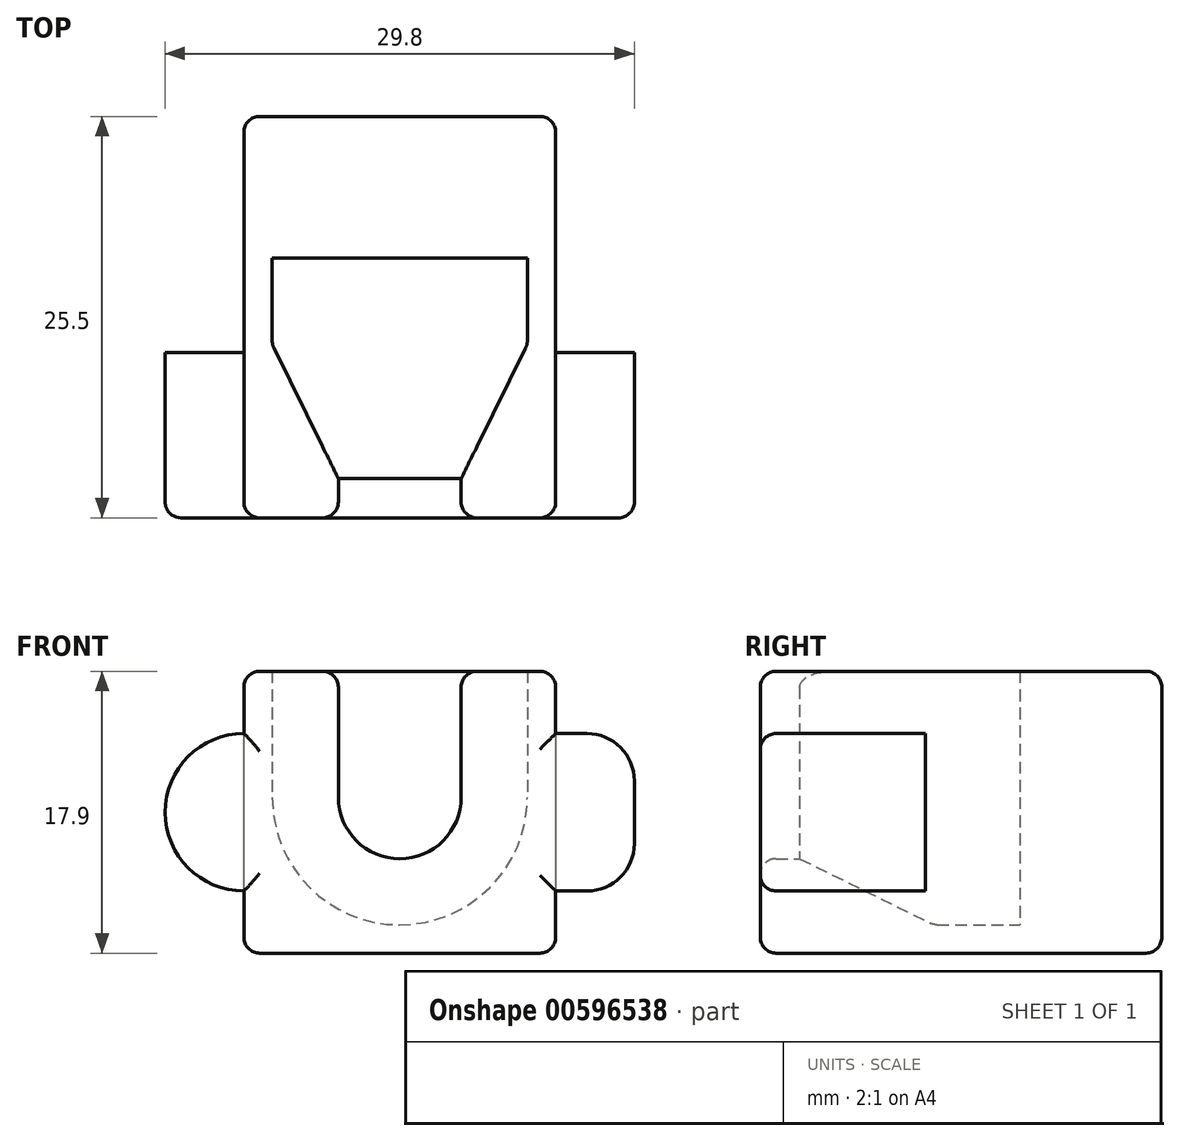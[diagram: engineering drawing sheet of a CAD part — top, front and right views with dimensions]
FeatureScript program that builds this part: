
annotation { "Feature Type Name" : "Feature", "Feature Type Description" : "" }
export const myFeature = defineFeature(function(context is Context, id is Id, definition is map)
    precondition{}
    {
        {
            var Q0;
            Q0=qCreatedBy(makeId("Top.planeOp"),FACE);
            var sketch = newSketch(context, id + "F0", { "sketchPlane" : qUnion([Q0])});
            skLineSegment(sketch, "E0", {"start": v(-9.9, 0) * mm, "end": v(-3.9, 0) * mm});
            skLineSegment(sketch, "E1", {"start": v(-3.9, 0) * mm, "end": v(-3.9, 2.5) * mm});
            skLineSegment(sketch, "E2", {"start": v(-3.9, 2.5) * mm, "end": v(-8.1, 11) * mm});
            skLineSegment(sketch, "E3", {"start": v(-8.1, 11) * mm, "end": v(-8.1, 16.5) * mm});
            skLineSegment(sketch, "E4", {"start": v(-8.1, 16.5) * mm, "end": v(0, 16.5) * mm});
            skLineSegment(sketch, "E5", {"start": v(0, 16.5) * mm, "end": v(0, 18.5) * mm});
            skLineSegment(sketch, "E6", {"start": v(0, 18.5) * mm, "end": v(-9.9, 18.5) * mm});
            skLineSegment(sketch, "E7", {"start": v(-9.9, 18.5) * mm, "end": v(-9.9, 0) * mm});
            skLineSegment(sketch, "E8", {"start": v(0, 44.18) * mm, "end": v(0, -54.71) * mm, "construction": true});
            skSolve(sketch);
        }
        {
            var Q0;
            Q0=makeQuery(id+"F0.imprint","IMPRINT",FACE,{"disambiguationData":[TD([[makeQuery(id+"F0.imprint","IMPRINT",EDGE,{"derivedFrom":sQuery(id+"F0.wireOp",EDGE,"E0")}),1.0]])]});
            var Q1;
            Q1=sQuery(id+"F0.wireOp",EDGE,"E8");
            revolve(context, id + "F1", {"entities" : qUnion([Q0]), "axis" : qUnion([Q1]), "revolveType" : RevolveType.ONE_DIRECTION, "angle" : 180 * degree});
        }
        {
            var Q0;
            Q0=makeQuery(id+"F1.opRevolve","SWEPT_FACE",FACE,{"disambiguationData":[OSD([sQuery(id+"F0.wireOp",EDGE,"E6")])]});
            var sketch = newSketch(context, id + "F2", { "sketchPlane" : qUnion([Q0])});
            skLineSegment(sketch, "E9", {"start": v(-9.9, 0) * mm, "end": v(-9.9, -9.9) * mm});
            skPoint(sketch, "E9.endSnap0", {"position": v(0, -9.9) * mm});
            skLineSegment(sketch, "E10", {"start": v(-9.9, -9.9) * mm, "end": v(9.9, -9.9) * mm});
            skLineSegment(sketch, "E11", {"start": v(9.9, -9.9) * mm, "end": v(9.9, 0) * mm});
            skSolve(sketch);
        }
        {
            var Q0;
            {var subQ0=sQuery(id+"F2.wireOp",EDGE,"E9");Q0=makeQuery(id+"F2.imprint","IMPRINT",FACE,{"disambiguationData":[TD([[makeQuery(id+"F2.imprint","IMPRINT",EDGE,{"derivedFrom":subQ0}),1.0]])]});}
            var Q1;
            {var subQ0=sQuery(id+"F2.wireOp",EDGE,"E11");Q1=makeQuery(id+"F2.imprint","IMPRINT",FACE,{"disambiguationData":[TD([[makeQuery(id+"F2.imprint","IMPRINT",EDGE,{"derivedFrom":subQ0}),1.0]])]});}
            var Q2;
            Q2=makeQuery(id+"F1.opRevolve","SWEPT_FACE",FACE,{"disambiguationData":[OSD([sQuery(id+"F0.wireOp",EDGE,"E0")])]});
            extrude(context, id + "F3", {"entities" : qUnion([Q0, Q1]), "operationType" : NewBodyOperationType.ADD, "endBound" : BoundingType.UP_TO_SURFACE, "oppositeDirection" : true, "depth" : 17 * mm, "endBoundEntityFace" : qUnion([Q2]), "offsetDistance" : 25 * mm});
        }
        {
            var Q0;
            Q0=makeQuery(id+"F1.opRevolve","CAP_FACE",FACE,{"disambiguationData":[OSD([sQuery(id+"F0.wireOp",EDGE,"E0"),sQuery(id+"F0.wireOp",EDGE,"E1"),sQuery(id+"F0.wireOp",EDGE,"E2"),sQuery(id+"F0.wireOp",EDGE,"E3"),sQuery(id+"F0.wireOp",EDGE,"E4"),sQuery(id+"F0.wireOp",EDGE,"E5"),sQuery(id+"F0.wireOp",EDGE,"E6"),sQuery(id+"F0.wireOp",EDGE,"E7")])],"isStart":false});
            extrude(context, id + "F4", {"entities" : qUnion([Q0]), "operationType" : NewBodyOperationType.ADD, "depth" : 8 * mm, "offsetDistance" : 25 * mm});
        }
        {
            var Q0;
            {var subQ0=sQuery(id+"F0.wireOp",EDGE,"E6");var subQ1=sQuery(id+"F2.wireOp",EDGE,"E10");var subQ2=sQuery(id+"F0.wireOp",EDGE,"E7");Q0=makeQuery(id+"F4.boolean.opBoolean","MERGE",FACE,{"derivedFrom":[makeQuery(id+"F3.boolean.opBoolean","MERGE",FACE,{"derivedFrom":[makeQuery(id+"F1.opRevolve","SWEPT_FACE",FACE,{"disambiguationData":[OSD([subQ0])]}),makeQuery(id+"F3.opExtrude","CAP_FACE",FACE,{"disambiguationData":[OSD([subQ0,subQ2,sQuery(id+"F2.wireOp",EDGE,"E9"),subQ1])],"isStart":true}),makeQuery(id+"F3.opExtrude","CAP_FACE",FACE,{"disambiguationData":[OSD([subQ0,subQ2,subQ1,sQuery(id+"F2.wireOp",EDGE,"E11")])],"isStart":true})]}),makeQuery(id+"F4.opExtrude","SWEPT_FACE",FACE,{"disambiguationData":[OSD([subQ0])]})]});}
            var sketch = newSketch(context, id + "F5", { "sketchPlane" : qUnion([Q0])});
            skCircle(sketch, "E12", {"center": v(9.9, -0.95) * mm, "radius": 5 * mm});
            skLineSegment(sketch, "E13.bottom", {"start": v(-11.9, 4.05) * mm, "end": v(-4.9, 4.05) * mm});
            skLineSegment(sketch, "E13.top", {"start": v(-11.9, -5.95) * mm, "end": v(-4.9, -5.95) * mm});
            skLineSegment(sketch, "E13.left", {"start": v(-14.9, 1.05) * mm, "end": v(-14.9, -2.95) * mm});
            skLineSegment(sketch, "E13.right", {"start": v(-4.9, 4.05) * mm, "end": v(-4.9, -5.95) * mm});
            skPoint(sketch, "E13.middle", {"position": v(-9.9, -0.95) * mm});
            skPoint(sketch, "E14.visualSharp", {"position": v(-14.9, -5.95) * mm});
            skArc(sketch, "E14.filletArc", {"start": v(-14.9, -2.95) * mm, "mid": v(-14.02, -5.07) * mm, "end": v(-11.9, -5.95) * mm});
            skPoint(sketch, "E15.visualSharp", {"position": v(-14.9, 4.05) * mm});
            skArc(sketch, "E15.filletArc", {"start": v(-11.9, 4.05) * mm, "mid": v(-14.02, 3.17) * mm, "end": v(-14.9, 1.05) * mm});
            skSolve(sketch);
        }
        {
            var Q0;
            {var subQ0=sQuery(id+"F5.wireOp",EDGE,"E12");var subQ1=sQuery(id+"F2.wireOp",EDGE,"E11");var subQ2=makeQuery(id+"F4.boolean.opBoolean","MERGE",EDGE,{"derivedFrom":[makeQuery(id+"F3.opExtrude","CAP_EDGE",EDGE,{"disambiguationData":[OSD([subQ1])],"isStart":true}),makeQuery(id+"F4.opExtrude","SWEPT_EDGE",EDGE,{"disambiguationData":[OSD([sQuery(id+"F0.wireOp",EDGE,"E6"),sQuery(id+"F0.wireOp",EDGE,"E7"),subQ1])]})]});var subQ3=makeQuery(id+"F5.imprint","INTERSECT",VERTEX,{"disambiguationData":[OD(0.0)],"derivedFrom":[subQ2,subQ0]});Q0=makeQuery(id+"F5.imprint","IMPRINT",FACE,{"disambiguationData":[TD([[makeQuery(id+"F5.imprint","IMPRINT",EDGE,{"disambiguationData":[TD([[subQ3,-1.0]])],"derivedFrom":subQ0}),1.0]])]});}
            var Q1;
            Q1=makeQuery(id+"F5.imprint","IMPRINT",FACE,{"disambiguationData":[TD([[makeQuery(id+"F5.imprint","IMPRINT",EDGE,{"derivedFrom":sQuery(id+"F5.wireOp",EDGE,"E13.left")}),1.0]])]});
            var Q2;
            {var subQ0=sQuery(id+"F0.wireOp",EDGE,"E0");Q2=makeQuery(id+"F4.boolean.opBoolean","MERGE",FACE,{"derivedFrom":[makeQuery(id+"F3.boolean.opBoolean","MERGE",FACE,{"derivedFrom":[makeQuery(id+"F1.opRevolve","SWEPT_FACE",FACE,{"disambiguationData":[OSD([subQ0])]}),makeQuery(id+"F3.opExtrude","CAP_FACE",FACE,{"disambiguationData":[OSD([subQ0]),OD(0.0)],"isStart":false}),makeQuery(id+"F3.opExtrude","CAP_FACE",FACE,{"disambiguationData":[OSD([subQ0]),OD(1.0)],"isStart":false})]}),makeQuery(id+"F4.opExtrude","SWEPT_FACE",FACE,{"disambiguationData":[OSD([subQ0]),TDD([makeQuery(id+"F1.opRevolve","CAP_EDGE",EDGE,{"disambiguationData":[OSD([subQ0])],"isStart":true})])]}),makeQuery(id+"F4.opExtrude","SWEPT_FACE",FACE,{"disambiguationData":[OSD([subQ0]),TDD([makeQuery(id+"F1.opRevolve","CAP_EDGE",EDGE,{"disambiguationData":[OSD([subQ0])],"isStart":false})])]})]});}
            extrude(context, id + "F6", {"entities" : qUnion([Q0, Q1]), "operationType" : NewBodyOperationType.ADD, "endBound" : BoundingType.UP_TO_SURFACE, "oppositeDirection" : true, "depth" : 25 * mm, "endBoundEntityFace" : qUnion([Q2]), "offsetDistance" : 25 * mm});
        }
        {
            var Q0;
            {var subQ0=sQuery(id+"F5.wireOp",EDGE,"E12");var subQ1=sQuery(id+"F2.wireOp",EDGE,"E11");var subQ2=makeQuery(id+"F4.boolean.opBoolean","MERGE",EDGE,{"derivedFrom":[makeQuery(id+"F3.opExtrude","CAP_EDGE",EDGE,{"disambiguationData":[OSD([subQ1])],"isStart":true}),makeQuery(id+"F4.opExtrude","SWEPT_EDGE",EDGE,{"disambiguationData":[OSD([sQuery(id+"F0.wireOp",EDGE,"E6"),sQuery(id+"F0.wireOp",EDGE,"E7"),subQ1])]})]});var subQ3=makeQuery(id+"F5.imprint","INTERSECT",VERTEX,{"disambiguationData":[OD(0.0)],"derivedFrom":[subQ2,subQ0]});Q0=makeQuery(id+"F5.imprint","IMPRINT",FACE,{"disambiguationData":[TD([[makeQuery(id+"F5.imprint","IMPRINT",EDGE,{"disambiguationData":[TD([[subQ3,-1.0]])],"derivedFrom":subQ0}),1.0]])]});}
            var Q1;
            Q1=makeQuery(id+"F5.imprint","IMPRINT",FACE,{"disambiguationData":[TD([[makeQuery(id+"F5.imprint","IMPRINT",EDGE,{"derivedFrom":sQuery(id+"F5.wireOp",EDGE,"E13.left")}),1.0]])]});
            extrude(context, id + "F7", {"entities" : qUnion([Q0, Q1]), "operationType" : NewBodyOperationType.REMOVE, "oppositeDirection" : true, "depth" : 8 * mm, "offsetDistance" : 25 * mm});
        }
        {
            var Q0;
            {var subQ0=sQuery(id+"F5.wireOp",EDGE,"E12");var subQ1=sQuery(id+"F2.wireOp",EDGE,"E11");var subQ2=makeQuery(id+"F4.boolean.opBoolean","MERGE",EDGE,{"derivedFrom":[makeQuery(id+"F3.opExtrude","CAP_EDGE",EDGE,{"disambiguationData":[OSD([subQ1])],"isStart":true}),makeQuery(id+"F4.opExtrude","SWEPT_EDGE",EDGE,{"disambiguationData":[OSD([sQuery(id+"F0.wireOp",EDGE,"E6"),sQuery(id+"F0.wireOp",EDGE,"E7"),subQ1])]})]});var subQ3=makeQuery(id+"F5.imprint","INTERSECT",VERTEX,{"disambiguationData":[OD(0.0)],"derivedFrom":[subQ2,subQ0]});Q0=makeQuery(id+"F5.imprint","IMPRINT",FACE,{"disambiguationData":[TD([[makeQuery(id+"F5.imprint","IMPRINT",EDGE,{"disambiguationData":[TD([[subQ3,1.0]])],"derivedFrom":subQ0}),1.0]])]});}
            var Q1;
            {var subQ0=sQuery(id+"F5.wireOp",EDGE,"E13.right");Q1=makeQuery(id+"F5.imprint","IMPRINT",FACE,{"disambiguationData":[TD([[makeQuery(id+"F5.imprint","IMPRINT",EDGE,{"derivedFrom":subQ0}),1.0]])]});}
            var Q2;
            {var subQ0=sQuery(id+"F5.wireOp",EDGE,"E13.right");Q2=makeQuery(id+"F5.imprint","IMPRINT",FACE,{"disambiguationData":[TD([[makeQuery(id+"F5.imprint","IMPRINT",EDGE,{"derivedFrom":subQ0}),-1.0]])]});}
            extrude(context, id + "F8", {"entities" : qUnion([Q0, Q1, Q2]), "operationType" : NewBodyOperationType.ADD, "depth" : 7 * mm, "offsetDistance" : 25 * mm});
        }
        {
            var Q0;
            Q0=makeQuery(id+"F4.opExtrude","CAP_EDGE",EDGE,{"disambiguationData":[OSD([sQuery(id+"F0.wireOp",EDGE,"E6"),sQuery(id+"F0.wireOp",EDGE,"E7"),sQuery(id+"F2.wireOp",EDGE,"E9")])],"isStart":false});
            var Q1;
            Q1=makeQuery(id+"F4.opExtrude","CAP_EDGE",EDGE,{"disambiguationData":[OSD([sQuery(id+"F0.wireOp",EDGE,"E6"),sQuery(id+"F0.wireOp",EDGE,"E7"),sQuery(id+"F2.wireOp",EDGE,"E11")])],"isStart":false});
            var Q2;
            Q2=makeQuery(id+"F3.opExtrude","SWEPT_EDGE",EDGE,{"disambiguationData":[OSD([sQuery(id+"F2.wireOp",EDGE,"E9"),sQuery(id+"F2.wireOp",EDGE,"E10")])]});
            var Q3;
            Q3=makeQuery(id+"F3.opExtrude","SWEPT_EDGE",EDGE,{"disambiguationData":[OSD([sQuery(id+"F2.wireOp",EDGE,"E10"),sQuery(id+"F2.wireOp",EDGE,"E11")])]});
            var Q4;
            {var subQ0=sQuery(id+"F0.wireOp",EDGE,"E0");Q4=makeQuery(id+"F4.opExtrude","CAP_EDGE",EDGE,{"disambiguationData":[OSD([subQ0]),TDD([makeQuery(id+"F1.opRevolve","CAP_EDGE",EDGE,{"disambiguationData":[OSD([subQ0])],"isStart":false})])],"isStart":false});}
            var Q5;
            {var subQ0=sQuery(id+"F0.wireOp",EDGE,"E0");Q5=makeQuery(id+"F4.opExtrude","CAP_EDGE",EDGE,{"disambiguationData":[OSD([subQ0]),TDD([makeQuery(id+"F1.opRevolve","CAP_EDGE",EDGE,{"disambiguationData":[OSD([subQ0])],"isStart":true})])],"isStart":false});}
            var Q6;
            {var subQ0=sQuery(id+"F2.wireOp",EDGE,"E9");Q6=makeQuery(id+"F4.boolean.opBoolean","MERGE",EDGE,{"derivedFrom":[makeQuery(id+"F3.opExtrude","CAP_EDGE",EDGE,{"disambiguationData":[OSD([subQ0])],"isStart":false}),makeQuery(id+"F4.opExtrude","SWEPT_EDGE",EDGE,{"disambiguationData":[OSD([sQuery(id+"F0.wireOp",EDGE,"E0"),sQuery(id+"F0.wireOp",EDGE,"E6"),sQuery(id+"F0.wireOp",EDGE,"E7"),subQ0])]})]});}
            var Q7;
            {var subQ0=sQuery(id+"F2.wireOp",EDGE,"E11");Q7=makeQuery(id+"F4.boolean.opBoolean","MERGE",EDGE,{"derivedFrom":[makeQuery(id+"F3.opExtrude","CAP_EDGE",EDGE,{"disambiguationData":[OSD([subQ0])],"isStart":false}),makeQuery(id+"F4.opExtrude","SWEPT_EDGE",EDGE,{"disambiguationData":[OSD([sQuery(id+"F0.wireOp",EDGE,"E0"),sQuery(id+"F0.wireOp",EDGE,"E6"),sQuery(id+"F0.wireOp",EDGE,"E7"),subQ0])]})]});}
            var Q8;
            {var subQ0=sQuery(id+"F2.wireOp",EDGE,"E10");Q8=makeQuery(id+"F3.boolean.opBoolean","MERGE",EDGE,{"derivedFrom":[makeQuery(id+"F3.opExtrude","CAP_EDGE",EDGE,{"disambiguationData":[OSD([subQ0]),TDD([makeQuery(id+"F2.imprint","IMPRINT",EDGE,{"disambiguationData":[TD([[makeQuery(id+"F2.imprint","INTERSECT",VERTEX,{"derivedFrom":[sQuery(id+"F2.wireOp",EDGE,"E9"),subQ0]}),-1.0]])],"derivedFrom":subQ0})])],"isStart":false}),makeQuery(id+"F3.opExtrude","CAP_EDGE",EDGE,{"disambiguationData":[OSD([subQ0]),TDD([makeQuery(id+"F2.imprint","IMPRINT",EDGE,{"disambiguationData":[TD([[makeQuery(id+"F2.imprint","INTERSECT",VERTEX,{"derivedFrom":[subQ0,sQuery(id+"F2.wireOp",EDGE,"E11")]}),1.0]])],"derivedFrom":subQ0})])],"isStart":false})]});}
            var Q9;
            {var subQ0=sQuery(id+"F0.wireOp",EDGE,"E6");var subQ1=sQuery(id+"F2.wireOp",EDGE,"E10");var subQ2=sQuery(id+"F0.wireOp",EDGE,"E7");Q9=makeQuery(id+"F4.boolean.opBoolean","MERGE",FACE,{"derivedFrom":[makeQuery(id+"F3.boolean.opBoolean","MERGE",FACE,{"derivedFrom":[makeQuery(id+"F1.opRevolve","SWEPT_FACE",FACE,{"disambiguationData":[OSD([subQ0])]}),makeQuery(id+"F3.opExtrude","CAP_FACE",FACE,{"disambiguationData":[OSD([subQ0,subQ2,sQuery(id+"F2.wireOp",EDGE,"E9"),subQ1])],"isStart":true}),makeQuery(id+"F3.opExtrude","CAP_FACE",FACE,{"disambiguationData":[OSD([subQ0,subQ2,subQ1,sQuery(id+"F2.wireOp",EDGE,"E11")])],"isStart":true})]}),makeQuery(id+"F4.opExtrude","SWEPT_FACE",FACE,{"disambiguationData":[OSD([subQ0])]})]});}
            var Q10;
            {var subQ0=sQuery(id+"F0.wireOp",EDGE,"E0");Q10=makeQuery(id+"F6.boolean.opBoolean","MERGE",FACE,{"derivedFrom":[makeQuery(id+"F4.boolean.opBoolean","MERGE",FACE,{"derivedFrom":[makeQuery(id+"F3.boolean.opBoolean","MERGE",FACE,{"derivedFrom":[makeQuery(id+"F1.opRevolve","SWEPT_FACE",FACE,{"disambiguationData":[OSD([subQ0])]}),makeQuery(id+"F3.opExtrude","CAP_FACE",FACE,{"disambiguationData":[OSD([subQ0]),OD(0.0)],"isStart":false}),makeQuery(id+"F3.opExtrude","CAP_FACE",FACE,{"disambiguationData":[OSD([subQ0]),OD(1.0)],"isStart":false})]}),makeQuery(id+"F4.opExtrude","SWEPT_FACE",FACE,{"disambiguationData":[OSD([subQ0]),TDD([makeQuery(id+"F1.opRevolve","CAP_EDGE",EDGE,{"disambiguationData":[OSD([subQ0])],"isStart":true})])]}),makeQuery(id+"F4.opExtrude","SWEPT_FACE",FACE,{"disambiguationData":[OSD([subQ0]),TDD([makeQuery(id+"F1.opRevolve","CAP_EDGE",EDGE,{"disambiguationData":[OSD([subQ0])],"isStart":false})])]})]}),makeQuery(id+"F6.opExtrude","CAP_FACE",FACE,{"disambiguationData":[OSD([subQ0]),OD(0.0)],"isStart":false}),makeQuery(id+"F6.opExtrude","CAP_FACE",FACE,{"disambiguationData":[OSD([subQ0]),OD(1.0)],"isStart":false})]});}
            var Q11;
            Q11=makeQuery(id+"F8.opExtrude","CAP_FACE",FACE,{"disambiguationData":[OSD([sQuery(id+"F0.wireOp",EDGE,"E6"),sQuery(id+"F0.wireOp",EDGE,"E7"),sQuery(id+"F2.wireOp",EDGE,"E9"),sQuery(id+"F2.wireOp",EDGE,"E10"),sQuery(id+"F2.wireOp",EDGE,"E11")])],"isStart":false});
            var Q12;
            Q12=makeQuery(id+"F7.boolean.opBoolean","COPY",EDGE,{"derivedFrom":makeQuery(id+"F7.opExtrude","CAP_EDGE",EDGE,{"disambiguationData":[OSD([sQuery(id+"F5.wireOp",EDGE,"E13.left")])],"isStart":false})});
            var Q13;
            Q13=makeQuery(id+"F7.boolean.opBoolean","COPY",EDGE,{"derivedFrom":makeQuery(id+"F7.opExtrude","CAP_EDGE",EDGE,{"disambiguationData":[OSD([sQuery(id+"F5.wireOp",EDGE,"E12")])],"isStart":false})});
            var Q14;
            {var subQ0=sQuery(id+"F0.wireOp",EDGE,"E1");Q14=makeQuery(id+"F4.opExtrude","CAP_EDGE",EDGE,{"disambiguationData":[OSD([subQ0]),TDD([makeQuery(id+"F1.opRevolve","CAP_EDGE",EDGE,{"disambiguationData":[OSD([subQ0])],"isStart":false})])],"isStart":false});}
            var Q15;
            {var subQ0=sQuery(id+"F0.wireOp",EDGE,"E1");Q15=makeQuery(id+"F4.opExtrude","CAP_EDGE",EDGE,{"disambiguationData":[OSD([subQ0]),TDD([makeQuery(id+"F1.opRevolve","CAP_EDGE",EDGE,{"disambiguationData":[OSD([subQ0])],"isStart":true})])],"isStart":false});}
            var Q16;
            {var subQ0=sQuery(id+"F0.wireOp",EDGE,"E3");var subQ1=sQuery(id+"F0.wireOp",EDGE,"E2");Q16=makeQuery(id+"F4.opExtrude","SWEPT_EDGE",EDGE,{"disambiguationData":[OSD([subQ1,subQ0]),TDD([makeQuery(id+"F1.opRevolve","CAP_VERTEX",VERTEX,{"disambiguationData":[OSD([subQ1,subQ0])],"isStart":true})])]});}
            fillet(context, id + "F9", {"entities" : qUnion([Q0, Q1, Q2, Q3, Q4, Q5, Q6, Q7, Q8, Q9, Q10, Q11, Q12, Q13, Q14, Q15, Q16]), "radius" : 1 * mm, "tangentPropagation" : true, "allowEdgeOverflow" : false});
        }
    });
